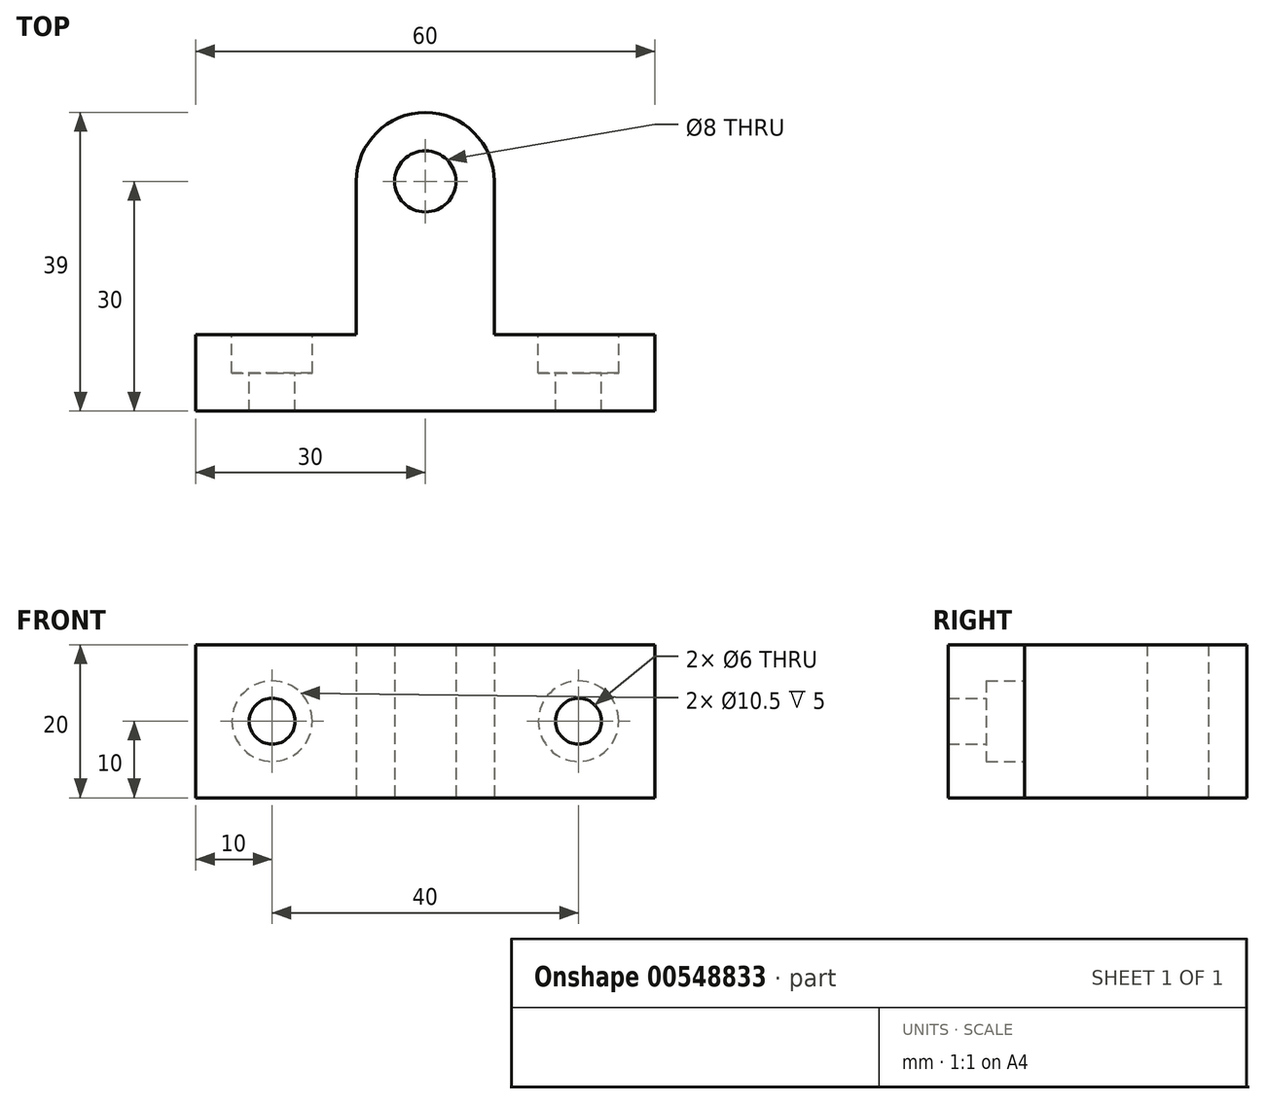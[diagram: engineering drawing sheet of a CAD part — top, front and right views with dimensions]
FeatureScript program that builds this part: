
annotation { "Feature Type Name" : "Feature", "Feature Type Description" : "" }
export const myFeature = defineFeature(function(context is Context, id is Id, definition is map)
    precondition{}
    {
        {
            var Q0;
            Q0=qCreatedBy(makeId("Top.planeOp"),FACE);
            var sketch = newSketch(context, id + "F0", { "sketchPlane" : qUnion([Q0])});
            skLineSegment(sketch, "E0.bottom", {"start": v(-30, 5) * mm, "end": v(30, 5) * mm});
            skLineSegment(sketch, "E0.top", {"start": v(-30, -5) * mm, "end": v(30, -5) * mm});
            skLineSegment(sketch, "E0.left", {"start": v(-30, 5) * mm, "end": v(-30, -5) * mm});
            skLineSegment(sketch, "E0.right", {"start": v(30, 5) * mm, "end": v(30, -5) * mm});
            skLineSegment(sketch, "E1.bottom", {"start": v(-9, 5) * mm, "end": v(9, 5) * mm});
            skLineSegment(sketch, "E1.left", {"start": v(-9, 5) * mm, "end": v(-9, 25) * mm});
            skLineSegment(sketch, "E1.right", {"start": v(9, 5) * mm, "end": v(9, 25) * mm});
            skArc(sketch, "E2", {"start": v(9, 25) * mm, "mid": v(0, 34) * mm, "end": v(-9, 25) * mm});
            skCircle(sketch, "E3", {"center": v(0, 25) * mm, "radius": 4 * mm});
            skSolve(sketch);
        }
        {
            var Q0;
            Q0 = qSketchRegion(id + "F0", true);
            extrude(context, id + "F1", {"entities" : qUnion([Q0]), "endBound" : BoundingType.SYMMETRIC, "depth" : 20 * mm, "offsetDistance" : 25 * mm});
        }
        {
            var Q0;
            {var subQ0=sQuery(id+"F0.wireOp",EDGE,"E0.bottom");Q0=makeQuery(id+"F1.opExtrude","SWEPT_FACE",FACE,{"disambiguationData":[OSD([subQ0]),TDD([makeQuery(id+"F0.imprint","IMPRINT",EDGE,{"disambiguationData":[TD([[makeQuery(id+"F0.imprint","INTERSECT",VERTEX,{"derivedFrom":[subQ0,sQuery(id+"F0.wireOp",EDGE,"E0.left")]}),-1.0]])],"derivedFrom":subQ0})])]});}
            var sketch = newSketch(context, id + "F2", { "sketchPlane" : qUnion([Q0])});
            skCircle(sketch, "E4", {"center": v(20, 0) * mm, "radius": 3 * mm});
            skCircle(sketch, "E5", {"center": v(-20, 0) * mm, "radius": 3 * mm});
            skCircle(sketch, "E6", {"center": v(20, 0) * mm, "radius": 5.25 * mm});
            skCircle(sketch, "E7", {"center": v(-20, 0) * mm, "radius": 5.25 * mm});
            skSolve(sketch);
        }
        {
            var Q0;
            Q0=makeQuery(id+"F2.imprint","IMPRINT",FACE,{"disambiguationData":[TD([[makeQuery(id+"F2.imprint","IMPRINT",EDGE,{"derivedFrom":sQuery(id+"F2.wireOp",EDGE,"E4")}),1.0]])]});
            var Q1;
            Q1=makeQuery(id+"F2.imprint","IMPRINT",FACE,{"disambiguationData":[TD([[makeQuery(id+"F2.imprint","IMPRINT",EDGE,{"derivedFrom":sQuery(id+"F2.wireOp",EDGE,"E5")}),1.0]])]});
            extrude(context, id + "F3", {"entities" : qUnion([Q0, Q1]), "operationType" : NewBodyOperationType.REMOVE, "endBound" : BoundingType.THROUGH_ALL, "oppositeDirection" : true, "depth" : 25 * mm, "offsetDistance" : 25 * mm});
        }
        {
            var Q0;
            Q0=makeQuery(id+"F2.imprint","IMPRINT",FACE,{"disambiguationData":[TD([[makeQuery(id+"F2.imprint","IMPRINT",EDGE,{"derivedFrom":sQuery(id+"F2.wireOp",EDGE,"E4")}),-1.0]])]});
            var Q1;
            Q1=makeQuery(id+"F2.imprint","IMPRINT",FACE,{"disambiguationData":[TD([[makeQuery(id+"F2.imprint","IMPRINT",EDGE,{"derivedFrom":sQuery(id+"F2.wireOp",EDGE,"E5")}),-1.0]])]});
            extrude(context, id + "F4", {"entities" : qUnion([Q0, Q1]), "operationType" : NewBodyOperationType.REMOVE, "oppositeDirection" : true, "depth" : 5 * mm, "offsetDistance" : 25 * mm});
        }
    });
